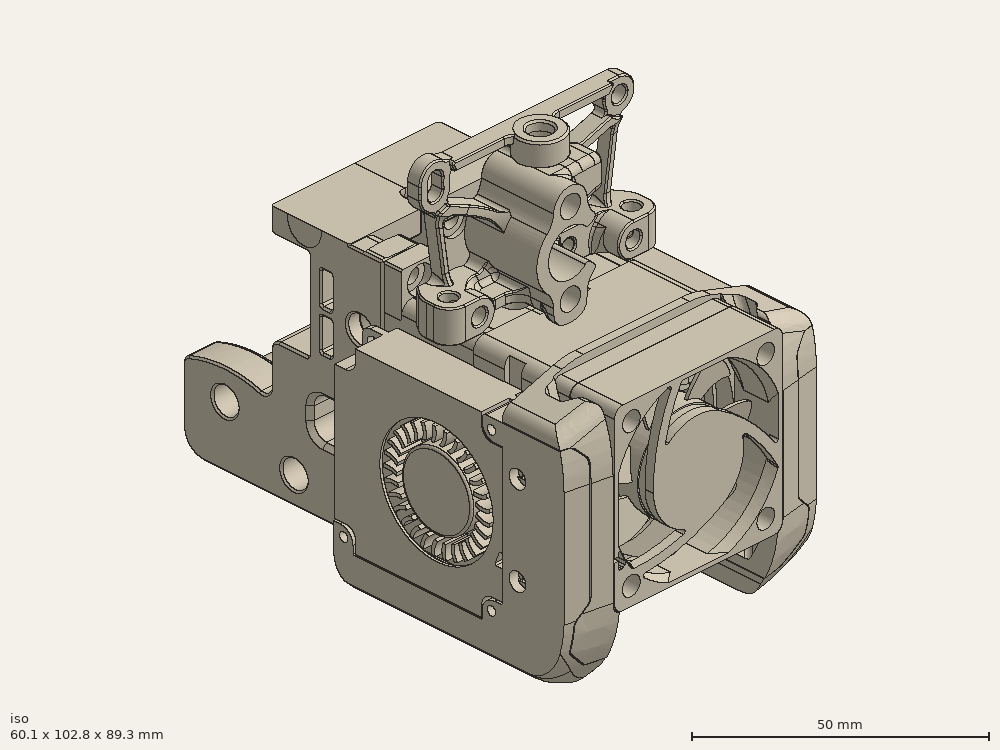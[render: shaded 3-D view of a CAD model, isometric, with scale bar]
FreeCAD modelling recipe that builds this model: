
FCSTD DOCUMENT  (FreeCAD 0.18R16146 (Git))
Label: dual4010
License: Other
LicenseURL: GPL3
objects: Part::Box×42, Part::Cylinder×41, Part::Cut×40, Part::MultiFuse×38, Part::Feature×21, Part::Chamfer×9, Part::Fillet×8, Mesh::Feature×2, Part::MultiCommon×1
note: 200 computed .brp shape members not serialized (recipe doc carries the construction recipe); baked Part::Feature solids carry a one-line shape summary decoded from their .brp

FEATURE [Part::Feature] Part__Feature376001  label="Left"
  shape: bbox 22.08 x 49.92 x 69.17 mm, 332 faces (baked)
FEATURE [Part::Feature] Part__Feature377001  label="Right"
  shape: bbox 22.32 x 49.92 x 69.17 mm, 357 faces (baked)
FEATURE [Part::Feature] Fusion003  label="mosquito"
  Placement = pos=(9e-15,-17.6,10.5) rot=(0.57735,0.57735,0.57735;2.0944rad)
  shape: bbox 27 x 18.85 x 47 mm, 463 faces, 0 solids (baked)
FEATURE [Part::Feature] Fusion036012039008  label="_2510-fan-pref"
  Placement = pos=(0.02,-24.2,26.5) rot=(1,0,0;1.5708rad)
  shape: bbox 25.76 x 10.5 x 25.8 mm, 132 faces, 2 solids (baked)
FEATURE [Part::Feature] Fusion001001  label="4010-fan"
  Placement = pos=(-19.9,-18.6,4.7) rot=(0,0,-1;1.5708rad)
  shape: bbox 10 x 40 x 40 mm, 256 faces, 2 solids (baked)
FEATURE [Part::Feature] Fusion036012039009  label="4010-fan001"
  Placement = pos=(19.9,-18.5,4.6) rot=(0,0,1;1.5708rad)
  shape: bbox 10 x 40 x 40 mm, 256 faces, 2 solids (baked)
FEATURE [Part::Box] Box001  label="2020"
  AttacherType = Attacher::AttachEngine3D
  Height = 20
  Length = 100
  Placement = pos=(-50,27.4,30.6) rot=(0,0,1;0rad)
  Width = 20
FEATURE [Mesh::Feature] orbitor2
  Placement = pos=(-6.35,-7.9,74.9) rot=(0,0,1;0rad)
FEATURE [Mesh::Feature] sherpa001  label="sherpa-mini"
  Placement = pos=(-4.3,-11.6,63.4) rot=(1,0,0;1.5708rad)
FEATURE [Part::Feature] Part__Feature013001  label="Cooling Fan Duct Focussed Edition_003"
  shape: bbox 15.53 x 56.74 x 51.73 mm, 120 faces (baked)
FEATURE [Part::Feature] Part__Feature012001  label="Cooling Fan Duct Focussed Edition001"
  shape: bbox 15.53 x 56.74 x 51.73 mm, 120 faces (baked)
FEATURE [Part::Feature] Part__Feature014001001  label="V6 Toolhead Mount 005"
  Placement = pos=(-0.05,0,0) rot=(0,0,1;0rad)
  shape: bbox 51.21 x 26.02 x 49.91 mm, 255 faces (baked)
FEATURE [Part::Feature] Part__Feature015001001  label="Front Plate Edwardyeeks002"
  shape: bbox 104.4 x 16.91 x 53.01 mm, 105 faces (baked)
FEATURE [Part::Feature] Part__Feature016001001  label="V6 Toolhead Mount 3 Front002"
  Placement = pos=(-0.05,0,0) rot=(0,0,1;0rad)
  shape: bbox 44.57 x 20.8 x 39.3 mm, 82 faces (baked)
FEATURE [Part::Box] Box  label="Cube"
  AttacherType = Attacher::AttachEngine3D
  Height = 10
  Length = 66
  Placement = pos=(-34,-27,49.86) rot=(0,0,1;0rad)
  Width = 34
FEATURE [Part::Box] Box002  label="Cube001"
  AttacherType = Attacher::AttachEngine3D
  Height = 10
  Length = 10
  Placement = pos=(-29.95,-23,41) rot=(0,0,1;0rad)
  Width = 26
FEATURE [Part::Box] Box004  label="Cube003"
  AttacherType = Attacher::AttachEngine3D
  Height = 10
  Length = 10
  Placement = pos=(20.05,-23,41) rot=(0,0,1;0rad)
  Width = 26
FEATURE [Part::Box] Box005  label="Cube004"
  AttacherType = Attacher::AttachEngine3D
  Height = 5.59
  Length = 24
  Placement = pos=(-12,-21.61,44.26) rot=(0,0,1;0rad)
  Width = 21.6
FEATURE [Part::Box] Box009  label="Cube008"
  AttacherType = Attacher::AttachEngine3D
  Height = 1.5
  Length = 24
  Placement = pos=(-12,-21.61,10.56) rot=(0,0,1;0rad)
  Width = 16
FEATURE [Part::Box] Box010  label="Cube009"
  AttacherType = Attacher::AttachEngine3D
  Height = 10
  Length = 25.3
  Placement = pos=(-12.65,-26.15,9.85) rot=(0,0,1;0rad)
  Width = 15
FEATURE [Part::Box] Box007  label="Cube006"
  AttacherType = Attacher::AttachEngine3D
  Height = 5.5
  Length = 30.3
  Placement = pos=(-15.15,-21.61,39) rot=(0,0,1;0rad)
  Width = 21.6
FEATURE [Part::Cylinder] Cylinder
  Angle = 360
  AttacherType = Attacher::AttachEngine3D
  Height = 22
  Placement = pos=(0,-17.6,33) rot=(0,0,1;0rad)
  Radius = 2.15
FEATURE [Part::Cylinder] Cylinder001
  Angle = 360
  AttacherType = Attacher::AttachEngine3D
  Height = 5
  Placement = pos=(-6,-17.6,33) rot=(0,0,1;0rad)
  Radius = 2.7
FEATURE [Part::Cylinder] Cylinder002
  Angle = 360
  AttacherType = Attacher::AttachEngine3D
  Height = 5
  Placement = pos=(6,-17.6,33) rot=(0,0,1;0rad)
  Radius = 2.7
FEATURE [Part::Cylinder] Cylinder003
  Angle = 360
  AttacherType = Attacher::AttachEngine3D
  Height = 22
  Placement = pos=(6,-17.6,33) rot=(0,0,1;0rad)
  Radius = 1.3
FEATURE [Part::Cylinder] Cylinder004
  Angle = 360
  AttacherType = Attacher::AttachEngine3D
  Height = 22
  Placement = pos=(-6,-17.6,33) rot=(0,0,1;0rad)
  Radius = 1.3
FEATURE [Part::MultiFuse] Fusion036012039011
  Shapes = -> [Cylinder,Cylinder003,Cylinder004]
FEATURE [Part::MultiFuse] Fusion036012039012
  Placement = pos=(0,0,11.9) rot=(0,0,1;0rad)
  Shapes = -> [Cylinder001,Cylinder002]
FEATURE [Part::Box] Box011  label="Cube010"
  AttacherType = Attacher::AttachEngine3D
  Height = 4.5
  Length = 12.15
  Placement = pos=(-18.65,-11.15,14) rot=(0,0,1;0rad)
  Width = 11.14
FEATURE [Part::Box] Box012  label="Cube011"
  AttacherType = Attacher::AttachEngine3D
  Height = 4.5
  Length = 12.15
  Placement = pos=(6.5,-11.15,14) rot=(0,0,1;0rad)
  Width = 11.14
FEATURE [Part::Box] Box013  label="Cube012"
  AttacherType = Attacher::AttachEngine3D
  Height = 10
  Length = 23.6
  Placement = pos=(-11.8,-22,4) rot=(0,0,1;0rad)
  Width = 11
FEATURE [Part::Fillet] Fillet
  Base = -> Box013
  Edges = 2 edges r=3: [Edge3,Edge7]
  Placement = pos=(0,2,0) rot=(0,0,1;0rad)
FEATURE [Part::Cylinder] Cylinder005
  Angle = 360
  AttacherType = Attacher::AttachEngine3D
  Height = 7
  Placement = pos=(16.1,-35.5,14.36) rot=(1,0,0;1.5708rad)
  Radius = 2.05
FEATURE [Part::Cylinder] Cylinder008
  Angle = 360
  AttacherType = Attacher::AttachEngine3D
  Height = 7
  Placement = pos=(-16.1,-35.5,14.36) rot=(1,0,0;1.5708rad)
  Radius = 2.05
FEATURE [Part::Cylinder] Cylinder009
  Angle = 360
  AttacherType = Attacher::AttachEngine3D
  Height = 8
  Placement = pos=(-16.1,-35.5,14.36) rot=(1,0,0;1.5708rad)
  Radius = 3.4
FEATURE [Part::Cylinder] Cylinder010
  Angle = 360
  AttacherType = Attacher::AttachEngine3D
  Height = 8
  Placement = pos=(-16.1,-35.5,46.21) rot=(1,0,0;1.5708rad)
  Radius = 3.4
FEATURE [Part::Cylinder] Cylinder011
  Angle = 360
  AttacherType = Attacher::AttachEngine3D
  Height = 8
  Placement = pos=(16.1,-35.5,46.21) rot=(1,0,0;1.5708rad)
  Radius = 3.4
FEATURE [Part::Cylinder] Cylinder012
  Angle = 360
  AttacherType = Attacher::AttachEngine3D
  Height = 8
  Placement = pos=(16.1,-35.5,14.36) rot=(1,0,0;1.5708rad)
  Radius = 3.4
FEATURE [Part::Cylinder] Cylinder013
  Angle = 360
  AttacherType = Attacher::AttachEngine3D
  Height = 21.6
  Placement = pos=(-16.1,-35.5,14.36) rot=(1,0,0;1.5708rad)
  Radius = 2
FEATURE [Part::Cylinder] Cylinder014
  Angle = 360
  AttacherType = Attacher::AttachEngine3D
  Height = 21.6
  Placement = pos=(-16.1,-35.5,46.21) rot=(1,0,0;1.5708rad)
  Radius = 2
FEATURE [Part::Cylinder] Cylinder015
  Angle = 360
  AttacherType = Attacher::AttachEngine3D
  Height = 21.6
  Placement = pos=(16.1,-35.5,46.21) rot=(1,0,0;1.5708rad)
  Radius = 2
FEATURE [Part::Cylinder] Cylinder016
  Angle = 360
  AttacherType = Attacher::AttachEngine3D
  Height = 21.6
  Placement = pos=(16.1,-35.5,14.36) rot=(1,0,0;1.5708rad)
  Radius = 2
FEATURE [Part::MultiFuse] Fusion036012039014
  Placement = pos=(0,35.49,0) rot=(0,0,1;0rad)
  Shapes = -> [Cylinder016,Cylinder015,Cylinder014,Cylinder013]
FEATURE [Part::MultiFuse] Fusion036012039016
  Placement = pos=(0,35.49,0) rot=(0,0,1;0rad)
  Shapes = -> [Cylinder012,Cylinder011,Cylinder010,Cylinder009]
FEATURE [Part::Cylinder] Cylinder017
  Angle = 360
  AttacherType = Attacher::AttachEngine3D
  Height = 10
  Placement = pos=(16.1,-35.5,14.36) rot=(1,0,0;1.5708rad)
  Radius = 1.7
FEATURE [Part::Cylinder] Cylinder019
  Angle = 360
  AttacherType = Attacher::AttachEngine3D
  Height = 10
  Placement = pos=(-16.1,-35.5,14.36) rot=(1,0,0;1.5708rad)
  Radius = 1.7
FEATURE [Part::Box] Box016  label="Cube015"
  AttacherType = Attacher::AttachEngine3D
  Height = 7
  Length = 1.2
  Placement = pos=(18.8,-21.61,42.8) rot=(0,0,1;0rad)
  Width = 14
FEATURE [Part::MultiFuse] Fusion036012039022
  Placement = pos=(0,23.89,0) rot=(0,0,1;0rad)
  Shapes = -> [Cylinder019,Cylinder017]
FEATURE [Part::MultiFuse] Fusion036012039023
  Placement = pos=(0,20.89,0) rot=(0,0,1;0rad)
  Shapes = -> [Cylinder005,Cylinder008]
FEATURE [Part::Cylinder] Cylinder020
  Angle = 360
  AttacherType = Attacher::AttachEngine3D
  Height = 10
  Placement = pos=(17.05,7,35) rot=(0.57735,-0.57735,0.57735;2.0944rad)
  Radius = 2.05
FEATURE [Part::Cylinder] Cylinder021
  Angle = 360
  AttacherType = Attacher::AttachEngine3D
  Height = 10
  Placement = pos=(-17.05,7,34) rot=(0.57735,-0.57735,0.57735;2.0944rad)
  Radius = 2.05
FEATURE [Part::Cylinder] Cylinder022
  Angle = 360
  AttacherType = Attacher::AttachEngine3D
  Height = 22.2
  Placement = pos=(-17.05,0,34) rot=(0.57735,-0.57735,0.57735;2.0944rad)
  Radius = 1.65
FEATURE [Part::Cylinder] Cylinder023
  Angle = 360
  AttacherType = Attacher::AttachEngine3D
  Height = 22.2
  Placement = pos=(17.05,8e-15,35) rot=(0.57735,-0.57735,0.57735;2.0944rad)
  Radius = 1.65
FEATURE [Part::Cylinder] Cylinder024
  Angle = 360
  AttacherType = Attacher::AttachEngine3D
  Height = 16
  Placement = pos=(-17.05,0,34) rot=(0.57735,-0.57735,0.57735;2.0944rad)
  Radius = 4
FEATURE [Part::Cylinder] Cylinder025
  Angle = 360
  AttacherType = Attacher::AttachEngine3D
  Height = 16
  Placement = pos=(17.05,8e-15,35) rot=(0.57735,-0.57735,0.57735;2.0944rad)
  Radius = 4
FEATURE [Part::Cut] Cut009
  Base = -> Part__Feature376001
  Tool = -> Cylinder021
FEATURE [Part::Cut] Cut010
  Base = -> Part__Feature377001
  Tool = -> Cylinder020
FEATURE [Part::MultiFuse] Fusion036012039025
  Shapes = -> [Cylinder024,Cylinder025]
FEATURE [Part::Box] Box017  label="Cube016"
  AttacherType = Attacher::AttachEngine3D
  Height = 10
  Length = 10
  Placement = pos=(17.9,-16,29) rot=(0,0,1;0rad)
  Width = 26
FEATURE [Part::Box] Box018  label="Cube017"
  AttacherType = Attacher::AttachEngine3D
  Height = 10
  Length = 10
  Placement = pos=(-27.9,-16,29) rot=(0,0,1;0rad)
  Width = 26
FEATURE [Part::MultiFuse] Fusion036012039026
  Shapes = -> [Box017,Box018]
FEATURE [Part::Cut] Cut011
  Base = -> Fusion036012039025
  Tool = -> Fusion036012039026
FEATURE [Part::MultiFuse] Fusion036012039028
  Shapes = -> [Cylinder022,Cylinder023]
FEATURE [Part::Cut] Cut
  Base = -> Part__Feature014001001
  Tool = -> Box
FEATURE [Part::MultiFuse] Fusion
  Shapes = -> [Box002,Box004]
FEATURE [Part::Cut] Cut012
  Base = -> Cut
  Tool = -> Fusion
FEATURE [Part::MultiFuse] Fusion036012039030
  Shapes = -> [Box005,Cut012]
FEATURE [Part::MultiFuse] Fusion036012039031
  Shapes = -> [Fusion036012039030,Box009]
FEATURE [Part::Cut] Cut013
  Base = -> Fusion036012039031
  Tool = -> Box010
FEATURE [Part::MultiFuse] Fusion036012039032
  Shapes = -> [Box007,Cut013]
FEATURE [Part::Cut] Cut014
  Base = -> Fusion036012039032
  Tool = -> Fusion036012039011
FEATURE [Part::Cut] Cut015
  Base = -> Cut014
  Tool = -> Fusion036012039012
FEATURE [Part::MultiFuse] Fusion036012039033
  Shapes = -> [Box011,Box012]
FEATURE [Part::MultiFuse] Fusion036012039034
  Shapes = -> [Cut015,Fusion036012039033]
FEATURE [Part::Chamfer] Chamfer
  Base = -> Fusion036012039034
  Edges = 2 edges r=2: [Edge94,Edge104]
FEATURE [Part::Cut] Cut016
  Base = -> Chamfer
  Tool = -> Fillet
FEATURE [Part::Chamfer] Chamfer001
  Base = -> Cut016
  Edges = 2 edges r=5: [Edge594,Edge678]
FEATURE [Part::MultiFuse] Fusion036012039035
  Shapes = -> [Fusion036012039014,Chamfer001]
FEATURE [Part::MultiFuse] Fusion036012039036
  Shapes = -> [Fusion036012039016,Fusion036012039035]
FEATURE [Part::Cut] Cut017
  Base = -> Fusion036012039036
  Tool = -> Fusion036012039022
FEATURE [Part::Cut] Cut018
  Base = -> Cut017
  Tool = -> Fusion036012039023
FEATURE [Part::MultiFuse] Fusion036012039037
  Shapes = -> [Box016,Cut018]
FEATURE [Part::Cylinder] Cylinder030
  Angle = 360
  AttacherType = Attacher::AttachEngine3D
  Height = 11
  Placement = pos=(16.25,11,9.41) rot=(1,0,0;1.5708rad)
  Radius = 2.5
FEATURE [Part::Cylinder] Cylinder031
  Angle = 360
  AttacherType = Attacher::AttachEngine3D
  Height = 11
  Placement = pos=(-16.25,11,9.41) rot=(1,0,0;1.5708rad)
  Radius = 2.5
FEATURE [Part::MultiFuse] Fusion036012039039
  Shapes = -> [Cut009,Cylinder031]
FEATURE [Part::MultiFuse] Fusion036012039040
  Shapes = -> [Cut010,Cylinder030]
FEATURE [Part::Box] Box019  label="Cube018"
  AttacherType = Attacher::AttachEngine3D
  Height = 10
  Length = 8.8
  Placement = pos=(11.2,-5,5) rot=(0,0,1;0rad)
  Width = 5
FEATURE [Part::Box] Box020  label="Cube019"
  AttacherType = Attacher::AttachEngine3D
  Height = 10
  Length = 8.8
  Placement = pos=(-20,-5,5) rot=(0,0,1;0rad)
  Width = 5
FEATURE [Part::Chamfer] Chamfer002
  Base = -> Box019
  Edges = 5 edges r=0.4: [Edge3,Edge4,Edge7,Edge8,Edge11]
FEATURE [Part::Chamfer] Chamfer003
  Base = -> Box020
  Edges = 5 edges r=0.4: [Edge3,Edge4,Edge7,Edge8,Edge11]
FEATURE [Part::Box] Box021  label="Cube020"
  AttacherType = Attacher::AttachEngine3D
  Height = 10
  Length = 26
  Placement = pos=(-13,-10,10.6) rot=(0,0,1;0rad)
  Width = 10
FEATURE [Part::Cylinder] Cylinder032
  Angle = 360
  AttacherType = Attacher::AttachEngine3D
  Height = 10
  Placement = pos=(-15.6,7,7.5) rot=(0.57735,-0.57735,0.57735;2.0944rad)
  Radius = 2.05
FEATURE [Part::Cylinder] Cylinder033
  Angle = 360
  AttacherType = Attacher::AttachEngine3D
  Height = 10
  Placement = pos=(15.6,7,7.5) rot=(0.57735,-0.57735,0.57735;2.0944rad)
  Radius = 2.05
FEATURE [Part::Cylinder] Cylinder034
  Angle = 360
  AttacherType = Attacher::AttachEngine3D
  Height = 10
  Placement = pos=(-15.6,2e-15,7.5) rot=(0.57735,-0.57735,0.57735;2.0944rad)
  Radius = 1.65
FEATURE [Part::Cylinder] Cylinder035
  Angle = 360
  AttacherType = Attacher::AttachEngine3D
  Height = 10
  Placement = pos=(15.6,0,7.5) rot=(0.57735,-0.57735,0.57735;2.0944rad)
  Radius = 1.65
FEATURE [Part::MultiFuse] Fusion036012039042
  Placement = pos=(0,3,0) rot=(0,0,1;0rad)
  Shapes = -> [Cylinder035,Cylinder034]
FEATURE [Part::MultiFuse] Fusion036012039043
  Shapes = -> [Chamfer003,Chamfer002]
FEATURE [Part::Cut] Cut021
  Base = -> Fusion036012039043
  Tool = -> Box021
FEATURE [Part::Cut] Cut023
  Base = -> Fusion036012039039
  Tool = -> Cylinder032
FEATURE [Part::Cut] Cut024
  Base = -> Fusion036012039040
  Tool = -> Cylinder033
FEATURE [Part::Box] Box023  label="Cube022"
  AttacherType = Attacher::AttachEngine3D
  Height = 10
  Length = 3.3
  Placement = pos=(-17.25,-6,-2.5) rot=(0,0,1;0rad)
  Width = 10
FEATURE [Part::Box] Box024  label="Cube023"
  AttacherType = Attacher::AttachEngine3D
  Height = 10
  Length = 3.3
  Placement = pos=(13.95,-8,-2.5) rot=(0,0,1;0rad)
  Width = 10
FEATURE [Part::MultiFuse] Fusion036012039045
  Shapes = -> [Box023,Box024]
FEATURE [Part::Feature] Fusion036012039029001  label="Fusion036012039046"
  Placement = pos=(0,-35.88,0) rot=(0,0,1;0rad)
  shape: bbox 40.1 x 10 x 7 mm, 6 faces, 2 solids (baked)
FEATURE [Part::Feature] Cut011001  label="Cut025"
  Placement = pos=(0,-21.61,0) rot=(0,0,1;0rad)
  shape: bbox 35.8 x 16 x 9 mm, 10 faces, 2 solids (baked)
FEATURE [Part::Feature] Cut011002  label="Cut026"
  Placement = pos=(0,-5.61,0) rot=(0,0,1;0rad)
  shape: bbox 35.8 x 16 x 9 mm, 10 faces, 2 solids (baked)
FEATURE [Part::MultiFuse] Fusion036012039029002
  Shapes = -> [Cut011,Cut011002,Fusion036012039037]
FEATURE [Part::MultiFuse] Fusion036012039029003
  Shapes = -> [Cut021,Fusion036012039029002]
FEATURE [Part::MultiFuse] Fusion036012039029004
  Shapes = -> [Fusion036012039045,Fusion036012039042]
FEATURE [Part::Cut] Cut011003
  Base = -> Fusion036012039029003
  Tool = -> Fusion036012039029004
FEATURE [Part::Feature] Fusion036012039028002  label="Fusion036012039029005"
  Placement = pos=(0,-18,0) rot=(0,0,1;0rad)
  shape: bbox 37.4 x 22.2 x 4.3 mm, 6 faces, 2 solids (baked)
FEATURE [Part::Cylinder] Cylinder036
  Angle = 360
  AttacherType = Attacher::AttachEngine3D
  Height = 10
  Placement = pos=(0,-35.88,32) rot=(1,0,0;1.5708rad)
  Radius = 22
FEATURE [Part::Cut] Cut011005
  Base = -> Cut011001
  Tool = -> Cylinder036
FEATURE [Part::MultiFuse] Fusion036012039029005  label="Fusion036012039029006"
  Shapes = -> [Cut011005,Part__Feature016001001]
FEATURE [Part::Cut] Cut011007
  Base = -> Fusion036012039029005
  Tool = -> Fusion036012039028002
FEATURE [Part::Cut] Cut011008
  Base = -> Cut011007
  Tool = -> Fusion036012039029001
FEATURE [Part::Box] Box025  label="Cube024"
  AttacherType = Attacher::AttachEngine3D
  Height = 25.15
  Length = 25.3
  Placement = pos=(-12.65,-24.25,13.85) rot=(0,0,1;0rad)
  Width = 10
FEATURE [Part::Cut] Cut011009
  Base = -> Cut011008
  Tool = -> Box025
FEATURE [Part::Box] Box026  label="Cube025"
  AttacherType = Attacher::AttachEngine3D
  Height = 25.6
  Length = 25.6
  Placement = pos=(-12.8,-40.1,8.7) rot=(0,0,1;0rad)
  Width = 19
FEATURE [Part::Cut] Cut011010
  Base = -> Cut011009
  Tool = -> Box026
FEATURE [Part::Chamfer] Chamfer004
  Base = -> Cut011010
  Edges = 2 edges r=1.8: [Edge76,Edge635]
FEATURE [Part::Box] Box027  label="Cube026"
  AttacherType = Attacher::AttachEngine3D
  Height = 36
  Length = 2
  Placement = pos=(18,-26,16) rot=(0,0,1;0rad)
  Width = 5
FEATURE [Part::Box] Box028  label="Cube027"
  AttacherType = Attacher::AttachEngine3D
  Height = 4
  Length = 2
  Placement = pos=(18,-25,16) rot=(0,0,1;0rad)
  Width = 22
FEATURE [Part::Box] Box029  label="Cube028"
  AttacherType = Attacher::AttachEngine3D
  Height = 4
  Length = 2
  Placement = pos=(18,-34,46) rot=(0,0,1;0rad)
  Width = 12
FEATURE [Part::MultiFuse] Fusion036012039029006  label="Fusion036012039029007"
  Placement = pos=(0.8,0,0) rot=(0,0,1;0rad)
  Shapes = -> [Box029,Box027]
FEATURE [Part::Fillet] Fillet001
  Base = -> Box028
  Edges = 2 edges r=1: [Edge11,Edge12]
  Placement = pos=(0.8,-0.6,0) rot=(0,0,1;0rad)
FEATURE [Part::Fillet] Fillet002
  Base = -> Fusion036012039029006
  Edges = 2 edges r=1: [Edge13,Edge24]
FEATURE [Part::Feature] Fillet001001  label="Fillet003"
  Placement = pos=(0.8,-0.6,8) rot=(0,0,1;0rad)
  shape: bbox 2 x 22 x 4 mm, 8 faces (baked)
FEATURE [Part::Box] Box030  label="Cube029"
  AttacherType = Attacher::AttachEngine3D
  Height = 28
  Length = 1.2
  Placement = pos=(18.8,-21.61,15.8) rot=(0,0,1;0rad)
  Width = 18
FEATURE [Part::Box] Box031  label="Cube030"
  AttacherType = Attacher::AttachEngine3D
  Height = 8
  Length = 2
  Placement = pos=(18.8,-7.61,17.9) rot=(0,0,1;0rad)
  Width = 4
FEATURE [Part::MultiFuse] Fusion036012039029007  label="Fusion036012039029008"
  Shapes = -> [Fillet001001,Box031,Fillet001]
FEATURE [Part::Fillet] Fillet001002
  Base = -> Fusion036012039029007
  Edges = 2 edges r=1: [Edge16,Edge30]
FEATURE [Part::Fillet] Fillet001003
  Base = -> Fillet002
  Edges = 1 edges r=1: [Edge7]
FEATURE [Part::Cut] Cut011015
  Base = -> Chamfer004
  Tool = -> Fillet001003
FEATURE [Part::Cut] Cut011016
  Base = -> Cut011003
  Tool = -> Fusion036012039028
FEATURE [Part::Box] Box032  label="Cube031"
  AttacherType = Attacher::AttachEngine3D
  Height = 6
  Length = 1.2
  Placement = pos=(20,-21.61,45.8) rot=(0,0,1;0rad)
  Width = 23
FEATURE [Part::MultiFuse] Fusion036012039029008  label="Fusion036012039029009"
  Shapes = -> [Box030,Cut011016]
FEATURE [Part::Cut] Cut011017
  Base = -> Fusion036012039029008
  Tool = -> Fillet001002
FEATURE [Part::Cut] Cut011018
  Base = -> Cut011017
  Tool = -> Box032
FEATURE [Part::Box] Box033  label="Cube032"
  AttacherType = Attacher::AttachEngine3D
  Height = 39
  Length = 2
  Placement = pos=(-20.8,-33.1,15) rot=(0,0,1;0rad)
  Width = 4
FEATURE [Part::Fillet] Fillet001004
  Base = -> Box033
  Edges = 2 edges r=1: [Edge9,Edge11]
FEATURE [Part::Cut] Cut011019
  Base = -> Cut011015
  Tool = -> Fillet001004
FEATURE [Part::Box] Box034  label="Cube033"
  AttacherType = Attacher::AttachEngine3D
  Height = 5.46
  Length = 12
  Placement = pos=(-6,-23.71,44.4) rot=(0,0,1;0rad)
  Width = 2.1
FEATURE [Part::MultiFuse] Fusion036012039029009  label="Fusion036012039029010"
  Shapes = -> [Box034,Cut011019]
FEATURE [Part::Feature] Cut001001  label="fan-spacer"
  Placement = pos=(0,-40.61,30) rot=(1,0,0;1.5708rad)
  shape: bbox 40 x 4 x 40 mm, 15 faces (baked)
FEATURE [Part::Feature] Part__Feature034  label="4010-fan002"
  Placement = pos=(-19.975,-55.3,50.05) rot=(-0.57735,-0.57735,0.57735;4.18879rad)
  shape: bbox 40.01 x 10.74 x 40.01 mm, 116 faces (baked)
FEATURE [Part::Feature] Cut001  label="fan-slot-cut"
  Placement = pos=(0,-40.61,30.2) rot=(1,0,0;1.5708rad)
  shape: bbox 40.5 x 25 x 40.5 mm, 15 faces (baked)
FEATURE [Part::Cut] Cut011020
  Base = -> Part__Feature015001001
  Tool = -> Cut001
FEATURE [Part::Cylinder] Cylinder037
  Angle = 360
  AttacherType = Attacher::AttachEngine3D
  Height = 20
  Placement = pos=(-9e-15,18.55,55.65) rot=(0.707107,0,0.707107;3.14159rad)
  Radius = 4
FEATURE [Part::Cylinder] Cylinder038
  Angle = 360
  AttacherType = Attacher::AttachEngine3D
  Height = 20
  Placement = pos=(-20,18.55,55.65) rot=(0.707107,0,0.707107;3.14159rad)
  Radius = 4
FEATURE [Part::MultiFuse] Fusion036012039029010  label="Fusion036012039029011"
  Shapes = -> [Cut024,Cylinder037]
FEATURE [Part::MultiFuse] Fusion036012039029011  label="Fusion036012039029012"
  Shapes = -> [Cut023,Cylinder038]
FEATURE [Part::Box] Box035  label="Cube034"
  AttacherType = Attacher::AttachEngine3D
  Height = 14
  Length = 60
  Placement = pos=(-30,0,56.3) rot=(0,0,1;0rad)
  Width = 36
FEATURE [Part::Box] Box036  label="Cube035"
  AttacherType = Attacher::AttachEngine3D
  Height = 14
  Length = 60
  Placement = pos=(-30,0,56.3) rot=(0,0,1;0rad)
  Width = 36
FEATURE [Part::Feature] Chamfer008016001  label="m8-probe-mount001"
  Placement = pos=(0,10,3) rot=(0,0,1;0rad)
  shape: bbox 15 x 15.5 x 10 mm, 61 faces (baked)
FEATURE [Part::Box] Box037  label="Cube036"
  AttacherType = Attacher::AttachEngine3D
  Height = 9
  Length = 30
  Placement = pos=(-15,-34.01,7.56) rot=(0,0,1;0rad)
  Width = 5
FEATURE [Part::Box] Box038  label="Cube037"
  AttacherType = Attacher::AttachEngine3D
  Height = 1
  Length = 30
  Placement = pos=(-15,-38.61,10.56) rot=(-1,0,0;5.93412rad)
  Width = 9
FEATURE [Part::Box] Box039  label="Cube038"
  AttacherType = Attacher::AttachEngine3D
  Height = 9
  Length = 30
  Placement = pos=(-15,-43.61,7.56) rot=(0,0,1;0rad)
  Width = 5
FEATURE [Part::Cut] Cut011023
  Base = -> Box038
  Tool = -> Box039
FEATURE [Part::Cut] Cut011024
  Base = -> Cut011023
  Tool = -> Box037
FEATURE [Part::MultiFuse] Fusion036012039029012  label="Fusion036012039029013"
  Shapes = -> [Cut011024,Fusion036012039029009]
FEATURE [Part::Cylinder] Cylinder039
  Angle = 360
  AttacherType = Attacher::AttachEngine3D
  Height = 10
  Placement = pos=(-15,18,50) rot=(0,0,1;0rad)
  Radius = 2
FEATURE [Part::Cylinder] Cylinder040
  Angle = 360
  AttacherType = Attacher::AttachEngine3D
  Height = 10
  Placement = pos=(15,18,50) rot=(0,0,1;0rad)
  Radius = 2
FEATURE [Part::MultiFuse] Fusion036012039029014  label="Fusion036012039029015"
  Placement = pos=(0,0,1.3) rot=(0,0,1;0rad)
  Shapes = -> [Cylinder040,Cylinder039]
FEATURE [Part::Box] Box040  label="Cube039"
  AttacherType = Attacher::AttachEngine3D
  Height = 9.8
  Length = 9.2
  Placement = pos=(-20,-4.51,46.5) rot=(0,0,1;0rad)
  Width = 4.5
FEATURE [Part::Box] Box041  label="Cube040"
  AttacherType = Attacher::AttachEngine3D
  Height = 9.8
  Length = 9.2
  Placement = pos=(10.8,-4.51,46.5) rot=(0,0,1;0rad)
  Width = 4.5
FEATURE [Part::Box] Box042  label="Cube041"
  AttacherType = Attacher::AttachEngine3D
  Height = 14
  Length = 21.6
  Placement = pos=(-10.8,-10.95,38) rot=(0,0,1;0rad)
  Width = 15
FEATURE [Part::Box] Box043  label="Cube042"
  AttacherType = Attacher::AttachEngine3D
  Height = 10
  Length = 10
  Placement = pos=(-27,-23,46.86) rot=(0,0,1;0rad)
  Width = 24
FEATURE [Part::Box] Box044  label="Cube043"
  AttacherType = Attacher::AttachEngine3D
  Height = 10
  Length = 10
  Placement = pos=(17,-23,46.86) rot=(0,0,1;0rad)
  Width = 24
FEATURE [Part::Box] Box045  label="Cube044"
  AttacherType = Attacher::AttachEngine3D
  Height = 10
  Length = 10
  Placement = pos=(-20,-23,39.86) rot=(0,0,1;0rad)
  Width = 24
FEATURE [Part::Box] Box046  label="Cube045"
  AttacherType = Attacher::AttachEngine3D
  Height = 10
  Length = 10
  Placement = pos=(10,-23,39.86) rot=(0,0,1;0rad)
  Width = 24
FEATURE [Part::Fillet] Fillet001005
  Base = -> Box045
  Edges = 1 edges r=2.8: [Edge2]
FEATURE [Part::Fillet] Fillet001006
  Base = -> Box046
  Edges = 1 edges r=2.8: [Edge6]
FEATURE [Part::Cut] Cut011025
  Base = -> Box043
  Tool = -> Fillet001005
FEATURE [Part::Cut] Cut011026
  Base = -> Box044
  Tool = -> Fillet001006
FEATURE [Part::MultiFuse] Fusion036012039029016  label="Fusion036012039029017"
  Shapes = -> [Cut011026,Cut011025]
FEATURE [Part::Cut] Cut011027
  Base = -> Cut011018
  Tool = -> Fusion036012039029016
FEATURE [Part::Chamfer] Chamfer008016002
  Base = -> Box041
  Edges = 5 edges r=0.4: [Edge2,Edge3,Edge6,Edge7,Edge12]
FEATURE [Part::Chamfer] Chamfer008016003
  Base = -> Box040
  Edges = 5 edges r=0.4: [Edge2,Edge3,Edge6,Edge7,Edge12]
FEATURE [Part::MultiFuse] Fusion036012039029017  label="Fusion036012039029018"
  Shapes = -> [Chamfer008016002,Chamfer008016003]
FEATURE [Part::MultiFuse] Fusion036012039029018  label="Fusion036012039029019"
  Shapes = -> [Fusion036012039029017,Cut011027]
FEATURE [Part::Cut] Cut011028
  Base = -> Fusion036012039029018
  Tool = -> Box042
FEATURE [Part::Chamfer] Chamfer008016004
  Base = -> Cut011028
  Edges = 2 edges r=3: [Edge28,Edge86]
FEATURE [Part::Cylinder] Cylinder041
  Angle = 360
  AttacherType = Attacher::AttachEngine3D
  Height = 10
  Placement = pos=(15.5,-2.5,52.71) rot=(1,0,0;1.5708rad)
  Radius = 3
FEATURE [Part::Cylinder] Cylinder042
  Angle = 360
  AttacherType = Attacher::AttachEngine3D
  Height = 10
  Placement = pos=(-15.5,-2.5,52.71) rot=(1,0,0;1.5708rad)
  Radius = 3
FEATURE [Part::Cylinder] Cylinder043
  Angle = 360
  AttacherType = Attacher::AttachEngine3D
  Height = 10
  Placement = pos=(-15.5,7,52.71) rot=(1,0,0;1.5708rad)
  Radius = 2.05
FEATURE [Part::Cylinder] Cylinder044
  Angle = 360
  AttacherType = Attacher::AttachEngine3D
  Height = 10
  Placement = pos=(15.5,7,52.71) rot=(1,0,0;1.5708rad)
  Radius = 2.05
FEATURE [Part::Cut] Cut011029
  Base = -> Fusion036012039029011
  Tool = -> Cylinder043
FEATURE [Part::Cut] Cut011030
  Base = -> Fusion036012039029010
  Tool = -> Cylinder044
FEATURE [Part::Cut] Cut011031
  Base = -> Cut011030
  Tool = -> Box035
FEATURE [Part::Cut] Cut011032
  Base = -> Cut011029
  Tool = -> Box036
FEATURE [Part::Cylinder] Cylinder045
  Angle = 360
  AttacherType = Attacher::AttachEngine3D
  Height = 10
  Placement = pos=(-15.5,1.2e-14,52.71) rot=(1,0,0;1.5708rad)
  Radius = 1.65
FEATURE [Part::Cylinder] Cylinder046
  Angle = 360
  AttacherType = Attacher::AttachEngine3D
  Height = 10
  Placement = pos=(15.5,1.2e-14,52.71) rot=(1,0,0;1.5708rad)
  Radius = 1.65
FEATURE [Part::Cut] Cut011033
  Base = -> Chamfer008016004
  Tool = -> Cylinder045
FEATURE [Part::Cut] Cut011034
  Base = -> Cut011033
  Tool = -> Cylinder046
FEATURE [Part::Cut] Cut011035
  Base = -> Cut011034
  Tool = -> Cylinder041
FEATURE [Part::Cut] Cut011036
  Base = -> Cut011035
  Tool = -> Cylinder042
FEATURE [Part::Box] Box047  label="Cube046"
  AttacherType = Attacher::AttachEngine3D
  Height = 10
  Length = 32
  Placement = pos=(-16,-38.61,39) rot=(0,0,1;0rad)
  Width = 17
FEATURE [Part::Chamfer] Chamfer008016005
  Base = -> Box047
  Edges = 1 edges: [Edge9 r1=9 r2=16.8]
FEATURE [Part::Cylinder] Cylinder047
  Angle = 360
  AttacherType = Attacher::AttachEngine3D
  Height = 44
  Placement = pos=(0,6.7,30) rot=(1,0,0;1.5708rad)
  Radius = 20
FEATURE [Part::MultiCommon] Common  label="air-router"
  Shapes = -> [Cylinder047,Chamfer008016005]
FEATURE [Part::Feature] Chamfer003001  label="sherpa-body-back"
  Placement = pos=(-4.3,-11.6,63.36) rot=(1,0,0;1.5708rad)
  shape: bbox 51.31 x 18.93 x 37.37 mm, 701 faces (baked)
